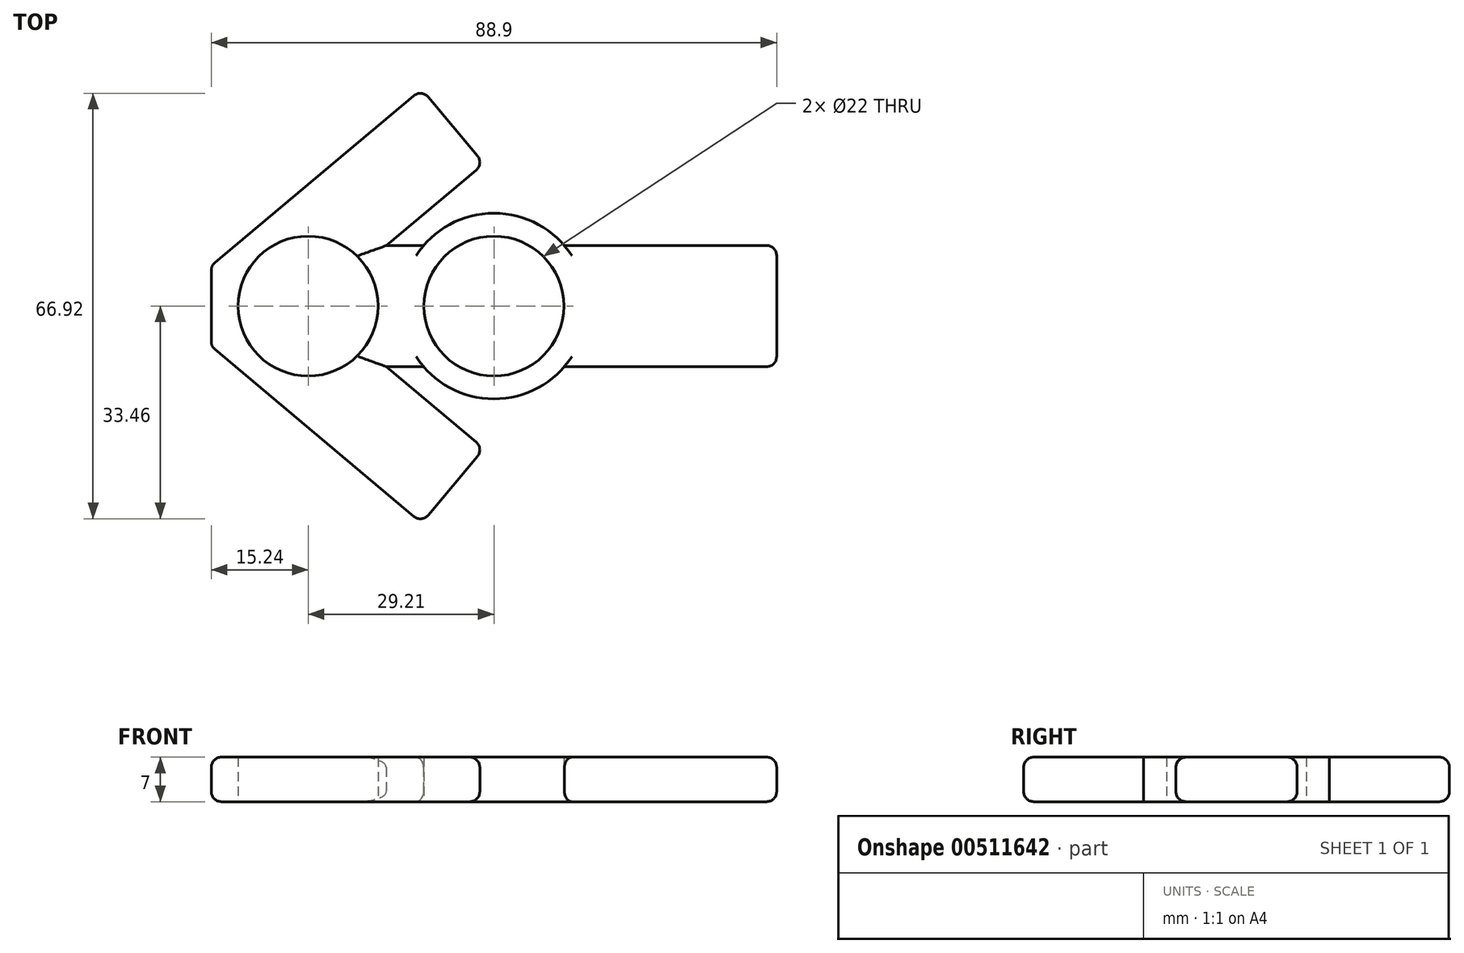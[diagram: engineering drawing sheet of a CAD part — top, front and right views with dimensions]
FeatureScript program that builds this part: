
annotation { "Feature Type Name" : "Feature", "Feature Type Description" : "" }
export const myFeature = defineFeature(function(context is Context, id is Id, definition is map)
    precondition{}
    {
        {
            var Q0;
            Q0=qCreatedBy(makeId("Top.planeOp"),FACE);
            var sketch = newSketch(context, id + "F0", { "sketchPlane" : qUnion([Q0])});
            skCircle(sketch, "E0", {"center": v(0, 0) * mm, "radius": 11 * mm});
            skLineSegment(sketch, "E1", {"start": v(0, 0) * mm, "end": v(-44.45, 0) * mm});
            skLineSegment(sketch, "E2", {"start": v(0, 0) * mm, "end": v(44.45, 0) * mm});
            skLineSegment(sketch, "E3", {"start": v(44.45, 0) * mm, "end": v(44.45, 9.53) * mm});
            skLineSegment(sketch, "E4", {"start": v(-44.45, 0) * mm, "end": v(-44.45, 6.35) * mm});
            skLineSegment(sketch, "E5", {"start": v(-44.45, 6.35) * mm, "end": v(-11.37, 34.1) * mm});
            skLineSegment(sketch, "E6", {"start": v(-11.37, 34.1) * mm, "end": v(-1.58, 22.43) * mm});
            skLineSegment(sketch, "E7", {"start": v(-1.58, 22.43) * mm, "end": v(-16.96, 9.52) * mm});
            skLineSegment(sketch, "E8", {"start": v(-16.96, 9.52) * mm, "end": v(44.45, 9.53) * mm});
            skCircle(sketch, "E9", {"center": v(-29.21, 0) * mm, "radius": 11 * mm});
            skCircle(sketch, "E10", {"center": v(0, 0) * mm, "radius": 14.6 * mm});
            skLineSegment(sketch, "E11.MirrorCS", {"start": v(-44.45, -6.35) * mm, "end": v(-11.37, -34.1) * mm});
            skLineSegment(sketch, "E12.MirrorCS", {"start": v(-11.37, -34.1) * mm, "end": v(-1.58, -22.43) * mm});
            skLineSegment(sketch, "E13.MirrorCS", {"start": v(-44.45, 0) * mm, "end": v(-44.45, -6.35) * mm});
            skLineSegment(sketch, "E14.MirrorCS", {"start": v(-16.96, -9.52) * mm, "end": v(44.45, -9.52) * mm});
            skLineSegment(sketch, "E15.MirrorCS", {"start": v(44.45, 0) * mm, "end": v(44.45, -9.52) * mm});
            skLineSegment(sketch, "E16.MirrorCS", {"start": v(-1.58, -22.43) * mm, "end": v(-16.96, -9.52) * mm});
            skSolve(sketch);
        }
        {
            var Q0;
            {var subQ0=sQuery(id+"F0.wireOp",EDGE,"E3");Q0=makeQuery(id+"F0.imprint","IMPRINT",FACE,{"disambiguationData":[TD([[makeQuery(id+"F0.imprint","IMPRINT",EDGE,{"derivedFrom":subQ0}),1.0]])]});}
            var Q1;
            {var subQ0=sQuery(id+"F0.wireOp",EDGE,"E15.MirrorCS");Q1=makeQuery(id+"F0.imprint","IMPRINT",FACE,{"disambiguationData":[TD([[makeQuery(id+"F0.imprint","IMPRINT",EDGE,{"derivedFrom":subQ0}),-1.0]])]});}
            var Q2;
            {var subQ1=sQuery(id+"F0.wireOp",EDGE,"E8");var subQ3=sQuery(id+"F0.wireOp",EDGE,"E0");var subQ4=makeQuery(id+"F0.imprint","INTERSECT",VERTEX,{"disambiguationData":[OD(0.0)],"derivedFrom":[subQ3,subQ1]});Q2=makeQuery(id+"F0.imprint","IMPRINT",FACE,{"disambiguationData":[TD([[makeQuery(id+"F0.imprint","IMPRINT",EDGE,{"disambiguationData":[TD([[subQ4,-1.0]])],"derivedFrom":subQ3}),-1.0]])]});}
            var Q3;
            {var subQ0=sQuery(id+"F0.wireOp",EDGE,"E14.MirrorCS");var subQ3=sQuery(id+"F0.wireOp",EDGE,"E0");var subQ5=makeQuery(id+"F0.imprint","INTERSECT",VERTEX,{"disambiguationData":[OD(0.0)],"derivedFrom":[subQ3,subQ0]});Q3=makeQuery(id+"F0.imprint","IMPRINT",FACE,{"disambiguationData":[TD([[makeQuery(id+"F0.imprint","IMPRINT",EDGE,{"disambiguationData":[TD([[subQ5,-1.0]])],"derivedFrom":subQ3}),-1.0]])]});}
            var Q4;
            Q4=makeQuery(id+"F0.imprint","IMPRINT",FACE,{"disambiguationData":[TD([[makeQuery(id+"F0.imprint","IMPRINT",EDGE,{"derivedFrom":sQuery(id+"F0.wireOp",EDGE,"E11.MirrorCS")}),1.0]])]});
            var Q5;
            {var subQ0=sQuery(id+"F0.wireOp",EDGE,"E8");var subQ1=sQuery(id+"F0.wireOp",EDGE,"E0");var subQ2=makeQuery(id+"F0.imprint","INTERSECT",VERTEX,{"disambiguationData":[OD(0.0)],"derivedFrom":[subQ1,subQ0]});Q5=makeQuery(id+"F0.imprint","IMPRINT",FACE,{"disambiguationData":[TD([[makeQuery(id+"F0.imprint","IMPRINT",EDGE,{"disambiguationData":[TD([[subQ2,1.0]])],"derivedFrom":subQ1}),-1.0]])]});}
            var Q6;
            {var subQ0=sQuery(id+"F0.wireOp",EDGE,"E8");var subQ3=sQuery(id+"F0.wireOp",EDGE,"E0");var subQ4=makeQuery(id+"F0.imprint","INTERSECT",VERTEX,{"disambiguationData":[OD(1.0)],"derivedFrom":[subQ3,subQ0]});Q6=makeQuery(id+"F0.imprint","IMPRINT",FACE,{"disambiguationData":[TD([[makeQuery(id+"F0.imprint","IMPRINT",EDGE,{"disambiguationData":[TD([[subQ4,-1.0]])],"derivedFrom":subQ3}),-1.0]])]});}
            var Q7;
            {var subQ3=sQuery(id+"F0.wireOp",EDGE,"E0");var subQ7=sQuery(id+"F0.wireOp",EDGE,"E1");var subQ9=makeQuery(id+"F0.imprint","INTERSECT",VERTEX,{"derivedFrom":[subQ3,subQ7]});Q7=makeQuery(id+"F0.imprint","IMPRINT",FACE,{"disambiguationData":[TD([[makeQuery(id+"F0.imprint","IMPRINT",EDGE,{"disambiguationData":[TD([[subQ9,-1.0]])],"derivedFrom":subQ3}),-1.0]])]});}
            var Q8;
            {var subQ0=sQuery(id+"F0.wireOp",EDGE,"E2");var subQ1=sQuery(id+"F0.wireOp",EDGE,"E0");var subQ2=makeQuery(id+"F0.imprint","INTERSECT",VERTEX,{"derivedFrom":[subQ1,subQ0]});Q8=makeQuery(id+"F0.imprint","IMPRINT",FACE,{"disambiguationData":[TD([[makeQuery(id+"F0.imprint","IMPRINT",EDGE,{"disambiguationData":[TD([[subQ2,1.0]])],"derivedFrom":subQ1}),-1.0]])]});}
            var Q9;
            {var subQ0=sQuery(id+"F0.wireOp",EDGE,"E4");Q9=makeQuery(id+"F0.imprint","IMPRINT",FACE,{"disambiguationData":[TD([[makeQuery(id+"F0.imprint","IMPRINT",EDGE,{"derivedFrom":subQ0}),-1.0]])]});}
            extrude(context, id + "F1", {"entities" : qUnion([Q0, Q1, Q2, Q3, Q4, Q5, Q6, Q7, Q8, Q9]), "depth" : 7 * mm});
        }
        {
            var Q0;
            Q0=makeQuery(id+"F1.opExtrude","SWEPT_FACE",FACE,{"disambiguationData":[OSD([sQuery(id+"F0.wireOp",EDGE,"E11.MirrorCS")])]});
            var Q1;
            Q1=makeQuery(id+"F1.opExtrude","SWEPT_FACE",FACE,{"disambiguationData":[OSD([sQuery(id+"F0.wireOp",EDGE,"E12.MirrorCS")])]});
            var Q2;
            Q2=makeQuery(id+"F1.opExtrude","SWEPT_FACE",FACE,{"disambiguationData":[OSD([sQuery(id+"F0.wireOp",EDGE,"E3"),sQuery(id+"F0.wireOp",EDGE,"E15.MirrorCS")])]});
            var Q3;
            Q3=makeQuery(id+"F1.opExtrude","SWEPT_FACE",FACE,{"disambiguationData":[OSD([sQuery(id+"F0.wireOp",EDGE,"E6")])]});
            var Q4;
            Q4=makeQuery(id+"F1.opExtrude","CAP_EDGE",EDGE,{"disambiguationData":[OSD([sQuery(id+"F0.wireOp",EDGE,"E4"),sQuery(id+"F0.wireOp",EDGE,"E13.MirrorCS")])],"isStart":false});
            var Q5;
            Q5=makeQuery(id+"F1.opExtrude","SWEPT_FACE",FACE,{"disambiguationData":[OSD([sQuery(id+"F0.wireOp",EDGE,"E4"),sQuery(id+"F0.wireOp",EDGE,"E13.MirrorCS")])]});
            var Q6;
            Q6=makeQuery(id+"F1.opExtrude","SWEPT_FACE",FACE,{"disambiguationData":[OSD([sQuery(id+"F0.wireOp",EDGE,"E5")])]});
            var Q7;
            Q7=makeQuery(id+"F1.opExtrude","CAP_EDGE",EDGE,{"disambiguationData":[OSD([sQuery(id+"F0.wireOp",EDGE,"E7")])],"isStart":false});
            var Q8;
            {var subQ0=sQuery(id+"F0.wireOp",EDGE,"E8");Q8=makeQuery(id+"F1.opExtrude","CAP_EDGE",EDGE,{"disambiguationData":[OSD([subQ0]),TDD([makeQuery(id+"F0.imprint","IMPRINT",EDGE,{"disambiguationData":[TD([[makeQuery(id+"F0.imprint","INTERSECT",VERTEX,{"derivedFrom":[sQuery(id+"F0.wireOp",EDGE,"E7"),subQ0]}),-1.0]])],"derivedFrom":subQ0})])],"isStart":false});}
            var Q9;
            Q9=makeQuery(id+"F1.opExtrude","CAP_EDGE",EDGE,{"disambiguationData":[OSD([sQuery(id+"F0.wireOp",EDGE,"E7")])],"isStart":true});
            var Q10;
            {var subQ0=sQuery(id+"F0.wireOp",EDGE,"E8");Q10=makeQuery(id+"F1.opExtrude","CAP_EDGE",EDGE,{"disambiguationData":[OSD([subQ0]),TDD([makeQuery(id+"F0.imprint","IMPRINT",EDGE,{"disambiguationData":[TD([[makeQuery(id+"F0.imprint","INTERSECT",VERTEX,{"derivedFrom":[sQuery(id+"F0.wireOp",EDGE,"E7"),subQ0]}),-1.0]])],"derivedFrom":subQ0})])],"isStart":true});}
            var Q11;
            {var subQ0=sQuery(id+"F0.wireOp",EDGE,"E10");var subQ1=sQuery(id+"F0.wireOp",EDGE,"E8");Q11=makeQuery(id+"F1.opExtrude","CAP_EDGE",EDGE,{"disambiguationData":[OSD([subQ0]),TDD([makeQuery(id+"F0.imprint","IMPRINT",EDGE,{"disambiguationData":[TD([[makeQuery(id+"F0.imprint","INTERSECT",VERTEX,{"disambiguationData":[OD(0.0)],"derivedFrom":[subQ1,subQ0]}),1.0]])],"derivedFrom":subQ0})])],"isStart":true});}
            var Q12;
            {var subQ0=sQuery(id+"F0.wireOp",EDGE,"E10");var subQ1=sQuery(id+"F0.wireOp",EDGE,"E8");Q12=makeQuery(id+"F1.opExtrude","CAP_EDGE",EDGE,{"disambiguationData":[OSD([subQ0]),TDD([makeQuery(id+"F0.imprint","IMPRINT",EDGE,{"disambiguationData":[TD([[makeQuery(id+"F0.imprint","INTERSECT",VERTEX,{"disambiguationData":[OD(0.0)],"derivedFrom":[subQ1,subQ0]}),1.0]])],"derivedFrom":subQ0})])],"isStart":false});}
            var Q13;
            {var subQ0=sQuery(id+"F0.wireOp",EDGE,"E8");Q13=makeQuery(id+"F1.opExtrude","CAP_EDGE",EDGE,{"disambiguationData":[OSD([subQ0]),TDD([makeQuery(id+"F0.imprint","IMPRINT",EDGE,{"disambiguationData":[TD([[makeQuery(id+"F0.imprint","INTERSECT",VERTEX,{"derivedFrom":[sQuery(id+"F0.wireOp",EDGE,"E3"),subQ0]}),1.0]])],"derivedFrom":subQ0})])],"isStart":false});}
            var Q14;
            {var subQ0=sQuery(id+"F0.wireOp",EDGE,"E8");Q14=makeQuery(id+"F1.opExtrude","CAP_EDGE",EDGE,{"disambiguationData":[OSD([subQ0]),TDD([makeQuery(id+"F0.imprint","IMPRINT",EDGE,{"disambiguationData":[TD([[makeQuery(id+"F0.imprint","INTERSECT",VERTEX,{"derivedFrom":[sQuery(id+"F0.wireOp",EDGE,"E3"),subQ0]}),1.0]])],"derivedFrom":subQ0})])],"isStart":true});}
            var Q15;
            {var subQ0=sQuery(id+"F0.wireOp",EDGE,"E14.MirrorCS");Q15=makeQuery(id+"F1.opExtrude","CAP_EDGE",EDGE,{"disambiguationData":[OSD([subQ0]),TDD([makeQuery(id+"F0.imprint","IMPRINT",EDGE,{"disambiguationData":[TD([[makeQuery(id+"F0.imprint","INTERSECT",VERTEX,{"derivedFrom":[subQ0,sQuery(id+"F0.wireOp",EDGE,"E15.MirrorCS")]}),1.0]])],"derivedFrom":subQ0})])],"isStart":false});}
            var Q16;
            {var subQ0=sQuery(id+"F0.wireOp",EDGE,"E14.MirrorCS");var subQ1=sQuery(id+"F0.wireOp",EDGE,"E10");Q16=makeQuery(id+"F1.opExtrude","CAP_EDGE",EDGE,{"disambiguationData":[OSD([subQ1]),TDD([makeQuery(id+"F0.imprint","IMPRINT",EDGE,{"disambiguationData":[TD([[makeQuery(id+"F0.imprint","INTERSECT",VERTEX,{"disambiguationData":[OD(0.0)],"derivedFrom":[subQ1,subQ0]}),-1.0]])],"derivedFrom":subQ1})])],"isStart":false});}
            var Q17;
            {var subQ0=sQuery(id+"F0.wireOp",EDGE,"E14.MirrorCS");Q17=makeQuery(id+"F1.opExtrude","CAP_EDGE",EDGE,{"disambiguationData":[OSD([subQ0]),TDD([makeQuery(id+"F0.imprint","IMPRINT",EDGE,{"disambiguationData":[TD([[makeQuery(id+"F0.imprint","INTERSECT",VERTEX,{"derivedFrom":[subQ0,sQuery(id+"F0.wireOp",EDGE,"E16.MirrorCS")]}),-1.0]])],"derivedFrom":subQ0})])],"isStart":false});}
            var Q18;
            Q18=makeQuery(id+"F1.opExtrude","CAP_EDGE",EDGE,{"disambiguationData":[OSD([sQuery(id+"F0.wireOp",EDGE,"E16.MirrorCS")])],"isStart":false});
            var Q19;
            Q19=makeQuery(id+"F1.opExtrude","CAP_EDGE",EDGE,{"disambiguationData":[OSD([sQuery(id+"F0.wireOp",EDGE,"E16.MirrorCS")])],"isStart":true});
            var Q20;
            {var subQ0=sQuery(id+"F0.wireOp",EDGE,"E14.MirrorCS");Q20=makeQuery(id+"F1.opExtrude","CAP_EDGE",EDGE,{"disambiguationData":[OSD([subQ0]),TDD([makeQuery(id+"F0.imprint","IMPRINT",EDGE,{"disambiguationData":[TD([[makeQuery(id+"F0.imprint","INTERSECT",VERTEX,{"derivedFrom":[subQ0,sQuery(id+"F0.wireOp",EDGE,"E15.MirrorCS")]}),1.0]])],"derivedFrom":subQ0})])],"isStart":true});}
            var Q21;
            {var subQ0=sQuery(id+"F0.wireOp",EDGE,"E14.MirrorCS");var subQ1=sQuery(id+"F0.wireOp",EDGE,"E10");Q21=makeQuery(id+"F1.opExtrude","CAP_EDGE",EDGE,{"disambiguationData":[OSD([subQ1]),TDD([makeQuery(id+"F0.imprint","IMPRINT",EDGE,{"disambiguationData":[TD([[makeQuery(id+"F0.imprint","INTERSECT",VERTEX,{"disambiguationData":[OD(0.0)],"derivedFrom":[subQ1,subQ0]}),-1.0]])],"derivedFrom":subQ1})])],"isStart":true});}
            var Q22;
            {var subQ0=sQuery(id+"F0.wireOp",EDGE,"E14.MirrorCS");Q22=makeQuery(id+"F1.opExtrude","CAP_EDGE",EDGE,{"disambiguationData":[OSD([subQ0]),TDD([makeQuery(id+"F0.imprint","IMPRINT",EDGE,{"disambiguationData":[TD([[makeQuery(id+"F0.imprint","INTERSECT",VERTEX,{"derivedFrom":[subQ0,sQuery(id+"F0.wireOp",EDGE,"E16.MirrorCS")]}),-1.0]])],"derivedFrom":subQ0})])],"isStart":true});}
            fillet(context, id + "F2", {"entities" : qUnion([Q0, Q1, Q2, Q3, Q4, Q5, Q6, Q7, Q8, Q9, Q10, Q11, Q12, Q13, Q14, Q15, Q16, Q17, Q18, Q19, Q20, Q21, Q22]), "radius" : 1.59 * mm, "tangentPropagation" : true, "allowEdgeOverflow" : false});
        }
    });
